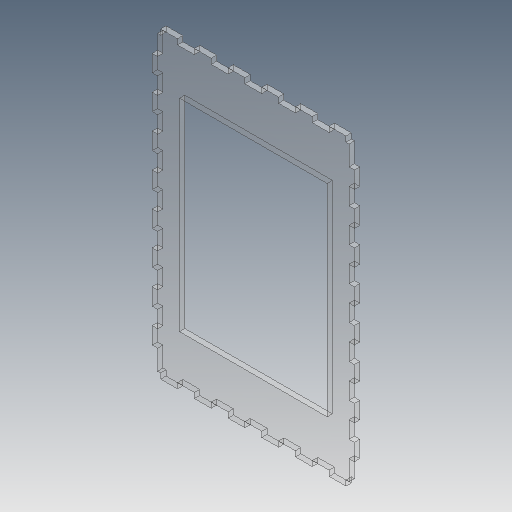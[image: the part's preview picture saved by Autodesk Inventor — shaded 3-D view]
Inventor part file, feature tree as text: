
AUTODESK INVENTOR PART (.ipt)
format: ipt  version: 2018 (Build 220112000, 112)  size: 342,016 bytes
history: native  units: mm
features: sketch x7, extrude x6, projected_geometry x5, pattern_linear x2, mirror x2, hole x1
ambient origin geometry x8: Origin, YZ Plane, XZ Plane, XY Plane, X Axis, Y Axis, Z Axis, Center Point
bodies: Solid1 (feature_tree)
feature tree (23):
  extrude  "Extrusion1"  Depth=180.0mm
  extrude  "Extrusion2"  TaperAngle=0.0deg  [1 undecoded]
  extrude  "Extrusion3"  Depth=3.175mm
  pattern_linear  "Rectangular Pattern1"  Count1=3  [1 undecoded]
  extrude  "Extrusion5"  Depth=1.5875mm
  mirror  "Mirror1"
  extrude  "Extrusion4"  Depth=1.5875mm
  pattern_linear  "Rectangular Pattern2"  Count1=4  [1 undecoded]
  extrude  "Extrusion6"  Depth=40.0mm
  mirror  "Mirror2"
  hole  "Hole1"  [1 undecoded]
  sketch  "Sketch1"  dims[d0=120.0mm d1=180.0mm]
  sketch  "Sketch2"  dims[d2=3.175mm d3=0.0mm]
  sketch  "Sketch3"  dims[d4=87.6mm d6=3.175mm]
  projected_geometry  "Projected Loop1"
  sketch  "Sketch4"  dims[d7=0.0mm d8=30.0mm]
  projected_geometry  "Projected Loop2"
  sketch  "Sketch5"  dims[d9=1.5875mm d10=1.5875mm]
  projected_geometry  "Projected Loop3"
  sketch  "Sketch6"  dims[d11=1.5875mm d12=1.5875mm]
  projected_geometry  "Projected Loop4"
  sketch  "Sketch7"  dims[d13=3.0mm d14=6.0mm d15=4.0mm d16=2.0mm d17=90.0deg d18=8.0mm d19=20.594885mm d20=40.0mm d21=40.0mm d22=36.0mm d24=36.0mm d25=10.0mm d26=15.0mm d27=3.175mm d28=10.0mm d29=0.0mm d30=60.0mm d32=20.0mm d33=3.175mm d34=5.0mm d35=10.0mm d36=0.0mm d37=0.0mm d38=90.0mm d40=20.0mm d41=10.0mm d42=3.175mm d43=10.0mm d44=0.0mm d45=10.0mm d46=0.0mm]
  projected_geometry  "Projected Loop5"
note: 4 required parameter values undecoded (feature->parameter linkage not recoverable at this tier; creation-order binding heuristic only, values carry confidence <= 0.55)
